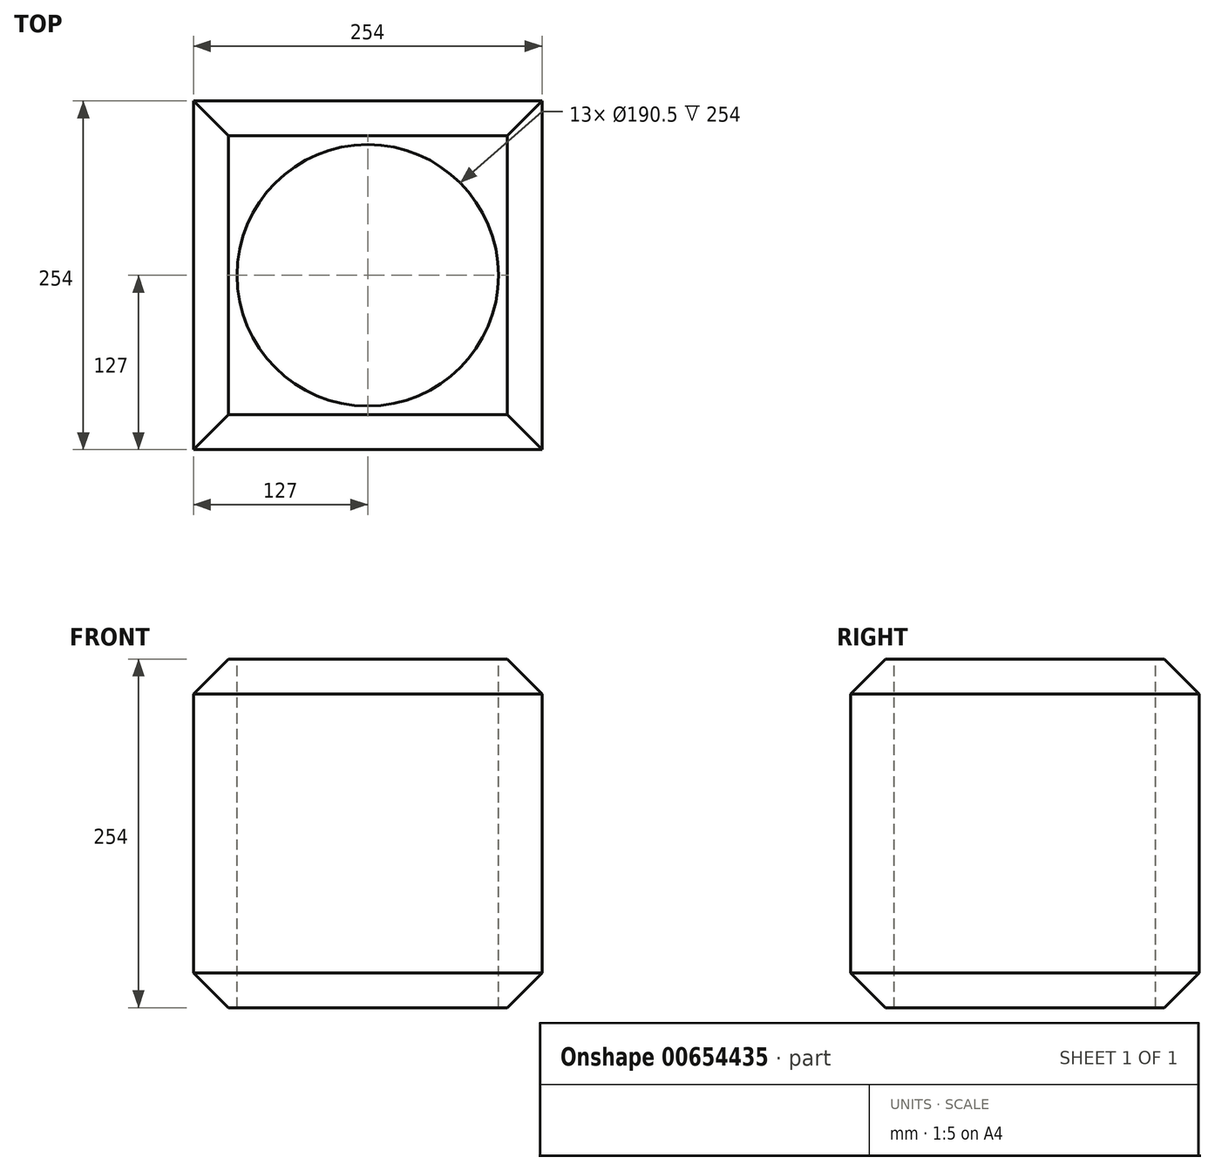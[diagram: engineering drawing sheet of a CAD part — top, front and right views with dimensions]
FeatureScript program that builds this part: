
annotation { "Feature Type Name" : "Feature", "Feature Type Description" : "" }
export const myFeature = defineFeature(function(context is Context, id is Id, definition is map)
    precondition{}
    {
        {
            var Q0;
            Q0=qCreatedBy(makeId("Top.planeOp"),FACE);
            var sketch = newSketch(context, id + "F0", { "sketchPlane" : qUnion([Q0])});
            skLineSegment(sketch, "E0", {"start": v(0, 0) * mm, "end": v(0, -254) * mm});
            skLineSegment(sketch, "E1", {"start": v(0, -254) * mm, "end": v(254, -254) * mm});
            skLineSegment(sketch, "E2", {"start": v(254, -254) * mm, "end": v(254, 0) * mm});
            skLineSegment(sketch, "E3", {"start": v(254, 0) * mm, "end": v(0, 0) * mm});
            skSolve(sketch);
        }
        {
            var Q0;
            Q0 = qSketchRegion(id + "F0", true);
            extrude(context, id + "F1", {"entities" : qUnion([Q0]), "depth" : 254 * mm, "offsetDistance" : 25.4 * mm});
        }
        {
            var Q0;
            Q0=makeQuery(id+"F1.opExtrude","CAP_FACE",FACE,{"disambiguationData":[OSD([sQuery(id+"F0.wireOp",EDGE,"E0"),sQuery(id+"F0.wireOp",EDGE,"E1"),sQuery(id+"F0.wireOp",EDGE,"E2"),sQuery(id+"F0.wireOp",EDGE,"E3")])],"isStart":false});
            var sketch = newSketch(context, id + "F2", { "sketchPlane" : qUnion([Q0])});
            skCircle(sketch, "E4", {"center": v(127, -127) * mm, "radius": 95.25 * mm});
            skPoint(sketch, "E4.centerSnap0", {"position": v(127, 0) * mm});
            skPoint(sketch, "E4.centerSnap1", {"position": v(0, -127) * mm});
            skSolve(sketch);
        }
        {
            var Q0;
            Q0 = qSketchRegion(id + "F2", true);
            extrude(context, id + "F3", {"entities" : qUnion([Q0]), "operationType" : NewBodyOperationType.REMOVE, "endBound" : BoundingType.THROUGH_ALL, "oppositeDirection" : true, "depth" : 25.4 * mm, "offsetDistance" : 25.4 * mm});
        }
        {
            var Q0;
            Q0=makeQuery(id+"F1.opExtrude","CAP_EDGE",EDGE,{"disambiguationData":[OSD([sQuery(id+"F0.wireOp",EDGE,"E1")])],"isStart":false});
            var Q1;
            Q1=makeQuery(id+"F1.opExtrude","CAP_EDGE",EDGE,{"disambiguationData":[OSD([sQuery(id+"F0.wireOp",EDGE,"E2")])],"isStart":false});
            var Q2;
            Q2=makeQuery(id+"F1.opExtrude","CAP_EDGE",EDGE,{"disambiguationData":[OSD([sQuery(id+"F0.wireOp",EDGE,"E3")])],"isStart":false});
            var Q3;
            Q3=makeQuery(id+"F1.opExtrude","CAP_EDGE",EDGE,{"disambiguationData":[OSD([sQuery(id+"F0.wireOp",EDGE,"E0")])],"isStart":false});
            var Q4;
            Q4=makeQuery(id+"F1.opExtrude","CAP_EDGE",EDGE,{"disambiguationData":[OSD([sQuery(id+"F0.wireOp",EDGE,"E2")])],"isStart":true});
            var Q5;
            Q5=makeQuery(id+"F1.opExtrude","CAP_EDGE",EDGE,{"disambiguationData":[OSD([sQuery(id+"F0.wireOp",EDGE,"E1")])],"isStart":true});
            var Q6;
            Q6=makeQuery(id+"F1.opExtrude","CAP_EDGE",EDGE,{"disambiguationData":[OSD([sQuery(id+"F0.wireOp",EDGE,"E3")])],"isStart":true});
            var Q7;
            Q7=makeQuery(id+"F1.opExtrude","CAP_EDGE",EDGE,{"disambiguationData":[OSD([sQuery(id+"F0.wireOp",EDGE,"E0")])],"isStart":true});
            chamfer(context, id + "F4", {"entities" : qUnion([Q0, Q1, Q2, Q3, Q4, Q5, Q6, Q7]), "width" : 25.4 * mm, "tangentPropagation" : true});
        }
    });
